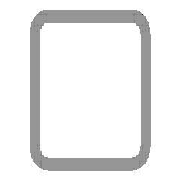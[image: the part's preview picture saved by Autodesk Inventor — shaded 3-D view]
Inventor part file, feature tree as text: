
AUTODESK INVENTOR PART (.ipt)
format: ipt  version: 2025.1 (Build 291241020, 241B)  size: 144,896 bytes
history: native  units: mm (DEFAULTED — no unit token found)
features: other x4, sketch x1, plane x1
ambient origin geometry x8: Origin, YZ Plane, XZ Plane, XY Plane, X Axis, Y Axis, Z Axis, Center Point
bodies: Solid1 (feature_tree), Body (feature_tree)
feature tree (6):
  parser-record x1  (decoder bookkeeping rows leaked as tree rows — omitted from the tree; the rows remain in map.json)
  other  "Driven Length"
  other  "Start Plane"
  other  "End Plane"
  sketch  "Sketch3"  dims[d3=1050.0mm d4=0.0mm d7=4.0mm d9=40.0mm d11=40.0mm d12=2.0mm d13=100.0mm d14=1150.0mm d15=20.0mm d16=20.0mm d17=90.0deg d18=1050.0mm]
  plane  "Work Plane3"
